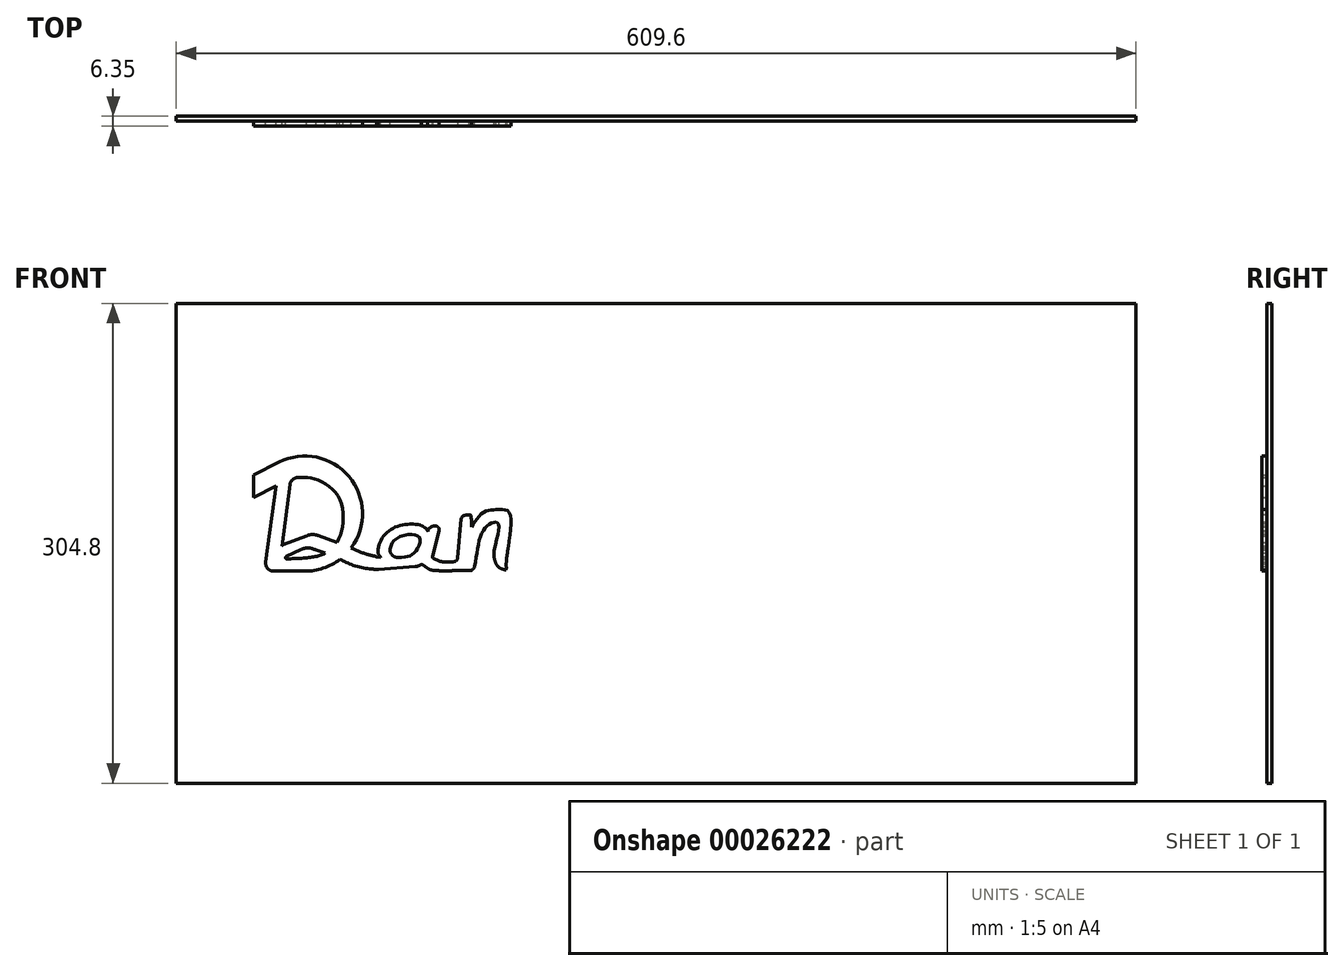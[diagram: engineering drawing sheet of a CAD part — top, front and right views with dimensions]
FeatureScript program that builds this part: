
annotation { "Feature Type Name" : "Feature", "Feature Type Description" : "" }
export const myFeature = defineFeature(function(context is Context, id is Id, definition is map)
    precondition{}
    {
        {
            var Q0;
            Q0=qCreatedBy(makeId("Front.planeOp"),FACE);
            var sketch = newSketch(context, id + "F0", { "sketchPlane" : qUnion([Q0])});
            skLineSegment(sketch, "E0.bottom", {"start": v(-304.36, 168.53) * mm, "end": v(305.24, 168.53) * mm});
            skLineSegment(sketch, "E0.top", {"start": v(-304.36, -136.27) * mm, "end": v(305.24, -136.27) * mm});
            skLineSegment(sketch, "E0.left", {"start": v(-304.36, 168.53) * mm, "end": v(-304.36, -136.27) * mm});
            skLineSegment(sketch, "E0.right", {"start": v(305.24, 168.53) * mm, "end": v(305.24, -136.27) * mm});
            skSolve(sketch);
        }
        {
            var Q0;
            Q0=makeQuery(id+"F0.imprint","IMPRINT",FACE,{"disambiguationData":[TD([[makeQuery(id+"F0.imprint","IMPRINT",EDGE,{"derivedFrom":sQuery(id+"F0.wireOp",EDGE,"E0.bottom")}),-1.0]])]});
            extrude(context, id + "F1", {"entities" : qUnion([Q0]), "depth" : 3.17 * mm});
        }
        {
            var Q0;
            Q0=makeQuery(id+"F1.opExtrude","CAP_FACE",FACE,{"disambiguationData":[OSD([sQuery(id+"F0.wireOp",EDGE,"E0.bottom"),sQuery(id+"F0.wireOp",EDGE,"E0.top"),sQuery(id+"F0.wireOp",EDGE,"E0.left"),sQuery(id+"F0.wireOp",EDGE,"E0.right")])],"isStart":false});
            var sketch = newSketch(context, id + "F2", { "sketchPlane" : qUnion([Q0])});
            skLineSegment(sketch, "E1", {"start": v(-258.66, -20.78) * mm, "end": v(-178.9, -20.78) * mm});
            skLineSegment(sketch, "E2", {"start": v(-178.9, -20.78) * mm, "end": v(-122.27, -20.78) * mm});
            skLineSegment(sketch, "E3", {"start": v(-122.27, -20.78) * mm, "end": v(-73.56, -20.78) * mm});
            skLineSegment(sketch, "E4", {"start": v(-73.56, -20.78) * mm, "end": v(-40.07, -20.78) * mm});
            skLineSegment(sketch, "E5", {"start": v(-40.07, -20.78) * mm, "end": v(1.94, -20.78) * mm});
            skLineSegment(sketch, "E6", {"start": v(1.94, -20.78) * mm, "end": v(38.48, -20.78) * mm});
            skLineSegment(sketch, "E7", {"start": v(104.84, -20.78) * mm, "end": v(209.57, -20.78) * mm});
            skLineSegment(sketch, "E8", {"start": v(-241.05, 52.49) * mm, "end": v(-247.54, 4.2) * mm});
            skLineSegment(sketch, "E9", {"start": v(-242.5, -1.56) * mm, "end": v(-222.66, -1.56) * mm});
            skArc(sketch, "E10", {"start": v(-222.66, -1.56) * mm, "mid": v(-210.96, 0.36) * mm, "end": v(-200.49, 5.93) * mm});
            skLineSegment(sketch, "E11", {"start": v(-239, 67.71) * mm, "end": v(-255.38, 59.52) * mm});
            skLineSegment(sketch, "E12", {"start": v(-258.22, 51) * mm, "end": v(-258.22, 51) * mm});
            skLineSegment(sketch, "E13", {"start": v(-249.7, 48.17) * mm, "end": v(-241.05, 52.49) * mm});
            skPoint(sketch, "E14.visualSharp", {"position": v(-261.06, 56.69) * mm});
            skLineSegment(sketch, "E14.filletArc", {"start": v(-255.38, 59.52) * mm, "end": v(-255.38, 59.52) * mm});
            skPoint(sketch, "E15.visualSharp", {"position": v(-255.38, 45.33) * mm});
            skLineSegment(sketch, "E16", {"start": v(-232.11, 53.5) * mm, "end": v(-237.18, 14.55) * mm});
            skFitSpline(sketch, "E17", {"points": [v(-231.6, 57.4) * mm, v(-217.7, 57.4) * mm, v(-201.48, 45.8) * mm, v(-199.6, 22.85) * mm, v(-210.9, 9.28) * mm, v(-238.3, 5.9) * mm], "startDerivative": vector(80.84, 11) * mm, "endDerivative": vector(-129.82, -10.44) * mm});
            skLineSegment(sketch, "E18", {"start": v(-214.13, 21.04) * mm, "end": v(-202.37, 16.67) * mm});
            skLineSegment(sketch, "E19", {"start": v(-234.45, 7.75) * mm, "end": v(-225.17, 12.17) * mm});
            skPoint(sketch, "E20.visualSharp", {"position": v(-219.31, 22.96) * mm});
            skArc(sketch, "E20.filletArc", {"start": v(-214.13, 21.04) * mm, "mid": v(-217.94, 21.67) * mm, "end": v(-221.7, 20.84) * mm});
            skPoint(sketch, "E21.visualSharp", {"position": v(-221.83, 13.76) * mm});
            skArc(sketch, "E21.filletArc", {"start": v(-215.7, 11.79) * mm, "mid": v(-220.38, 13.16) * mm, "end": v(-225.17, 12.17) * mm});
            skArc(sketch, "E22.filletArc", {"start": v(-234.45, 7.75) * mm, "mid": v(-234.9, 6.8) * mm, "end": v(-234.06, 6.19) * mm});
            skLineSegment(sketch, "E23", {"start": v(-236.14, 15.3) * mm, "end": v(-221.7, 20.84) * mm});
            skPoint(sketch, "E24.visualSharp", {"position": v(-238.12, 14.54) * mm});
            skArc(sketch, "E24.filletArc", {"start": v(-236.14, 15.3) * mm, "mid": v(-236.7, 15) * mm, "end": v(-237.18, 14.55) * mm});
            skPoint(sketch, "E25.visualSharp", {"position": v(-248.31, -1.56) * mm});
            skArc(sketch, "E25.filletArc", {"start": v(-247.54, 4.2) * mm, "mid": v(-246.33, 0.18) * mm, "end": v(-242.5, -1.56) * mm});
            skArc(sketch, "E26.filletArc", {"start": v(-227.57, 57.9) * mm, "mid": v(-230.61, 56.5) * mm, "end": v(-232.11, 53.5) * mm});
            skArc(sketch, "E27.trimOffspring", {"start": v(-193.22, 13.32) * mm, "mid": v(-194.68, 58.55) * mm, "end": v(-239, 67.71) * mm});
            skLineSegment(sketch, "E28", {"start": v(-248.31, -1.56) * mm, "end": v(-16.1, -1.56) * mm});
            skLineSegment(sketch, "E29", {"start": v(-174.55, 7.27) * mm, "end": v(-174.55, 7.27) * mm});
            skLineSegment(sketch, "E30", {"start": v(-144.66, 24.23) * mm, "end": v(-144.32, 23.55) * mm});
            skLineSegment(sketch, "E31", {"start": v(-144.66, 24.23) * mm, "end": v(-144.56, 24.4) * mm});
            skLineSegment(sketch, "E32", {"start": v(-140.06, 27.13) * mm, "end": v(-139.82, 27.13) * mm});
            skLineSegment(sketch, "E33", {"start": v(-137.36, 23.96) * mm, "end": v(-141.49, 7.85) * mm});
            skLineSegment(sketch, "E34", {"start": v(-175.71, -0.37) * mm, "end": v(-152.57, 1.35) * mm});
            skPoint(sketch, "E35.visualSharp", {"position": v(-171.6, 22.3) * mm});
            skPoint(sketch, "E36.visualSharp", {"position": v(-159.73, 28.33) * mm});
            skPoint(sketch, "E37.visualSharp", {"position": v(-146.1, 27.13) * mm});
            skArc(sketch, "E37.filletArc", {"start": v(-144.32, 23.55) * mm, "mid": v(-146, 25.78) * mm, "end": v(-148.38, 27.25) * mm});
            skFitSpline(sketch, "E38", {"points": [v(-177.38, 7.4) * mm, v(-174.92, 16.9) * mm, v(-168.37, 24.67) * mm, v(-158.5, 28.09) * mm, v(-148.48, 27.3) * mm, v(-145.04, 24.47) * mm], "startDerivative": vector(14.97, 44.13) * mm, "endDerivative": vector(24.1, -23.67) * mm});
            skPoint(sketch, "E36.filletArc.start.orphan", {"position": v(-158.5, 28.25) * mm});
            skArc(sketch, "E39.filletArc", {"start": v(-176.2, 12.3) * mm, "mid": v(-176.3, 11.09) * mm, "end": v(-176.1, 9.89) * mm});
            skFitSpline(sketch, "E40.trimOffspring", {"points": [v(-177.38, 7.4) * mm, v(-159.35, 7.4) * mm, v(-152.3, 11.02) * mm, v(-150.02, 20.15) * mm, v(-164, 19.4) * mm, v(-169.39, 7.4) * mm], "startDerivative": vector(65.48, -2.7) * mm, "endDerivative": vector(-5.68, -72.53) * mm});
            skArc(sketch, "E41.filletArc", {"start": v(-168.65, 12.49) * mm, "mid": v(-167.22, 8.64) * mm, "end": v(-163.42, 7.1) * mm});
            skPoint(sketch, "E42.visualSharp", {"position": v(-175.96, -0.4) * mm});
            skArc(sketch, "E42.filletArc", {"start": v(-175.88, -0.38) * mm, "mid": v(-175.8, -0.38) * mm, "end": v(-175.71, -0.37) * mm});
            skPoint(sketch, "E43.visualSharp", {"position": v(-151.52, 1.42) * mm});
            skArc(sketch, "E43.filletArc", {"start": v(-152.57, 1.35) * mm, "mid": v(-150.4, 1.83) * mm, "end": v(-148.46, 2.93) * mm});
            skLineSegment(sketch, "E44", {"start": v(-148.46, 2.93) * mm, "end": v(-143.95, -0.12) * mm});
            skLineSegment(sketch, "E45", {"start": v(-125.42, -1) * mm, "end": v(-118.5, -1) * mm});
            skPoint(sketch, "E46.visualSharp", {"position": v(-143.14, 27.13) * mm});
            skArc(sketch, "E46.filletArc", {"start": v(-140.06, 27.13) * mm, "mid": v(-142.7, 26.4) * mm, "end": v(-144.56, 24.4) * mm});
            skPoint(sketch, "E47.visualSharp", {"position": v(-136.55, 27.13) * mm});
            skArc(sketch, "E47.filletArc", {"start": v(-137.36, 23.96) * mm, "mid": v(-137.81, 26.15) * mm, "end": v(-139.82, 27.13) * mm});
            skLineSegment(sketch, "E48", {"start": v(-140.78, 6.37) * mm, "end": v(-137.44, 4.88) * mm});
            skLineSegment(sketch, "E49", {"start": v(-135.36, 4.44) * mm, "end": v(-128.15, 4.44) * mm});
            skPoint(sketch, "E50.visualSharp", {"position": v(-141.75, 6.8) * mm});
            skArc(sketch, "E50.filletArc", {"start": v(-141.49, 7.85) * mm, "mid": v(-141.4, 6.98) * mm, "end": v(-140.78, 6.37) * mm});
            skPoint(sketch, "E51.visualSharp", {"position": v(-136.45, 4.44) * mm});
            skArc(sketch, "E51.filletArc", {"start": v(-137.44, 4.88) * mm, "mid": v(-136.42, 4.55) * mm, "end": v(-135.36, 4.44) * mm});
            skPoint(sketch, "E52.visualSharp", {"position": v(-142.66, -1) * mm});
            skArc(sketch, "E52.filletArc", {"start": v(-143.95, -0.12) * mm, "mid": v(-142.6, -0.77) * mm, "end": v(-141.1, -1) * mm});
            skLineSegment(sketch, "E53", {"start": v(-125.62, 6.75) * mm, "end": v(-123.35, 31.61) * mm});
            skFitSpline(sketch, "E54", {"points": [v(-123.22, 33.06) * mm, v(-117.8, 34.24) * mm, v(-117.07, 33.06) * mm, v(-117.25, 0.6) * mm, v(-118.47, 0.65) * mm, v(-119.67, 0.72) * mm], "startDerivative": vector(22.26, 15.51) * mm, "endDerivative": vector(-0.04, -1.27) * mm});
            skArc(sketch, "E55.filletArc", {"start": v(-121.53, 33.82) * mm, "mid": v(-122.78, 33) * mm, "end": v(-123.35, 31.61) * mm});
            skFitSpline(sketch, "E56", {"points": [v(-116.66, 26.37) * mm, v(-109.03, 35.88) * mm, v(-100.72, 37.5) * mm, v(-92.58, 35.26) * mm, v(-94.73, 4.1) * mm, v(-95.63, -1.76) * mm, v(-102.81, -1.31) * mm, v(-103.75, 3.28) * mm], "startDerivative": vector(33.25, 69.65) * mm, "endDerivative": vector(14.9, 68.7) * mm});
            skFitSpline(sketch, "E57", {"points": [v(-118.5, -1) * mm, v(-116.53, -0.9) * mm, v(-114.8, 1.56) * mm], "startDerivative": vector(15.85, -0.5) * mm, "endDerivative": vector(2.08, 8.35) * mm});
            skFitSpline(sketch, "E58", {"points": [v(-114.8, 1.56) * mm, v(-110.55, 22.03) * mm, v(-104.07, 29) * mm, v(-99.86, 28.7) * mm, v(-103.75, 3.28) * mm], "startDerivative": vector(13.3, 66.56) * mm, "endDerivative": vector(-11.02, -98.62) * mm});
            skLineSegment(sketch, "E59", {"start": v(-215.7, 11.79) * mm, "end": v(-209.7, 9.85) * mm});
            skFitSpline(sketch, "E60", {"points": [v(-141.1, -1) * mm, v(-133.6, -1.4) * mm, v(-125.42, -1) * mm], "startDerivative": vector(15.17, -1.2) * mm, "endDerivative": vector(16.18, 1.19) * mm});
            skFitSpline(sketch, "E61", {"points": [v(-176.1, 9.89) * mm, v(-175.1, 8.08) * mm, v(-174.55, 7.27) * mm], "startDerivative": vector(0.37, -4.15) * mm, "endDerivative": vector(1.47, -2) * mm});
            skFitSpline(sketch, "E62", {"points": [v(-193.22, 13.32) * mm, v(-182.84, 9.1) * mm, v(-174.55, 7.27) * mm], "startDerivative": vector(18.02, -11.47) * mm, "endDerivative": vector(17.6, -2.48) * mm});
            skPoint(sketch, "E63.filletArc.start.orphan", {"position": v(-177.84, 7.6) * mm});
            skFitSpline(sketch, "E64", {"points": [v(-200.49, 5.93) * mm, v(-190.96, 1.92) * mm, v(-179.32, -0.32) * mm, v(-175.71, -0.37) * mm], "startDerivative": vector(23.23, -11.3) * mm, "endDerivative": vector(13.59, 0.56) * mm});
            skPoint(sketch, "E65.orphan", {"position": v(-177.2, -0.02) * mm});
            skLineSegment(sketch, "E66", {"start": v(-255.38, 59.52) * mm, "end": v(-255.38, 45.33) * mm});
            skLineSegment(sketch, "E67", {"start": v(-255.38, 45.33) * mm, "end": v(-249.7, 48.17) * mm});
            skLineSegment(sketch, "E68", {"start": v(-41.61, -1.56) * mm, "end": v(-22.9, -1.56) * mm});
            skLineSegment(sketch, "E69", {"start": v(26.94, -1.56) * mm, "end": v(3.48, -1.56) * mm});
            skPoint(sketch, "E70.visualSharp", {"position": v(-125.83, 4.44) * mm});
            skArc(sketch, "E70.filletArc", {"start": v(-128.15, 4.44) * mm, "mid": v(-126.44, 5.1) * mm, "end": v(-125.62, 6.75) * mm});
            skFitSpline(sketch, "E71", {"points": [v(-94.1, 9.75) * mm, v(-83.44, 6.64) * mm, v(-70.42, 10.65) * mm, v(-64.06, 33.22) * mm, v(-63.09, 35.02) * mm], "startDerivative": vector(36.38, -14.95) * mm, "endDerivative": vector(9.01, 9.22) * mm});
            skFitSpline(sketch, "E72", {"points": [v(-94.87, -0.81) * mm, v(-83.8, -1.04) * mm, v(-67.72, 0.93) * mm, v(-59.07, 25.1) * mm], "startDerivative": vector(38.4, -6.5) * mm, "endDerivative": vector(12.22, 74.4) * mm});
            skFitSpline(sketch, "E73", {"points": [v(-94.87, -0.81) * mm, v(-99.51, 0.94) * mm, v(-101.28, 3.28) * mm, v(-103.13, 7.6) * mm, v(-102.38, 11.5) * mm], "startDerivative": vector(-18.6, 2.38) * mm, "endDerivative": vector(1.13, 5.84) * mm});
            skLineSegment(sketch, "E74.trimOffspring", {"start": v(-94.87, -0.81) * mm, "end": v(-94.87, -0.81) * mm});
            skArc(sketch, "E75.filletArc", {"start": v(-93.46, 13.85) * mm, "mid": v(-92.8, 10.4) * mm, "end": v(-90.05, 8.23) * mm});
            skFitSpline(sketch, "E76", {"points": [v(-63.09, 35.02) * mm, v(-57.44, 36.05) * mm, v(-54.28, 35.02) * mm, v(-51.85, 11.25) * mm, v(-40.86, 6.71) * mm], "startDerivative": vector(31.2, 5.93) * mm, "endDerivative": vector(51.98, 11.21) * mm});
            skFitSpline(sketch, "E77", {"points": [v(-60.73, 15.8) * mm, v(-60.73, 5.25) * mm, v(-52.67, -0.47) * mm, v(-39.08, -0.61) * mm], "startDerivative": vector(-5.48, -36.42) * mm, "endDerivative": vector(39.62, 5.16) * mm});
            skLineSegment(sketch, "E78", {"start": v(-16.31, 5.69) * mm, "end": v(-15.07, 5.3) * mm});
            skFitSpline(sketch, "E79", {"points": [v(-39.08, -0.61) * mm, v(-20.1, 2.5) * mm, v(-0.98, 18.6) * mm, v(4.93, 31.72) * mm, v(0.26, 39.65) * mm, v(-18.15, 40.81) * mm, v(-33.46, 26.75) * mm, v(-36.41, 9.19) * mm], "startDerivative": vector(127, 3.04) * mm, "endDerivative": vector(-3.68, -124.36) * mm});
            skFitSpline(sketch, "E80", {"points": [v(-25.53, 9.5) * mm, v(-12.25, 19.21) * mm, v(-3.54, 28.85) * mm, v(-4.63, 33.2) * mm, v(-15.82, 31.95) * mm, v(-26, 22.48) * mm, v(-27.24, 10.98) * mm], "startDerivative": vector(66.91, 46.47) * mm, "endDerivative": vector(2.96, -70.75) * mm});
            skLineSegment(sketch, "E81", {"start": v(-40.86, 6.71) * mm, "end": v(-36.41, 8.24) * mm});
            skLineSegment(sketch, "E82", {"start": v(-25.56, 9.53) * mm, "end": v(-25.53, 9.5) * mm});
            skArc(sketch, "E83.filletArc", {"start": v(-27.32, 13.24) * mm, "mid": v(-27.07, 11.77) * mm, "end": v(-26.4, 10.44) * mm});
            skArc(sketch, "E84.filletArc", {"start": v(-26.4, 10.44) * mm, "mid": v(-25.57, 9.92) * mm, "end": v(-24.63, 10.13) * mm});
            skArc(sketch, "E85", {"start": v(-36.08, 15.9) * mm, "mid": v(-35.97, 12.14) * mm, "end": v(-34.46, 8.7) * mm});
            skLineSegment(sketch, "E86", {"start": v(-36.41, 8.24) * mm, "end": v(-34.46, 8.7) * mm});
            skFitSpline(sketch, "E87", {"points": [v(-102.38, 11.5) * mm, v(-102.38, 6.8) * mm, v(-101.28, 3.28) * mm], "startDerivative": vector(-0.62, -9.24) * mm, "endDerivative": vector(2.9, -7.16) * mm});
            skLineSegment(sketch, "E88.trimOffspring", {"start": v(-103.13, 7.6) * mm, "end": v(-103.13, 7.6) * mm});
            skLineSegment(sketch, "E89", {"start": v(22.18, -1.56) * mm, "end": v(3.48, -1.56) * mm});
            skLineSegment(sketch, "E90", {"start": v(-16.1, -1.56) * mm, "end": v(-22.72, 1.48) * mm});
            skFitSpline(sketch, "E91", {"points": [v(-13.76, 6.18) * mm, v(-0.92, 5.73) * mm, v(13.5, 11.45) * mm, v(30.63, 40.62) * mm, v(40.3, 65.41) * mm, v(47.88, 67.75) * mm, v(55.12, 60.88) * mm, v(49.49, 63.56) * mm], "startDerivative": vector(95.62, -9.36) * mm, "endDerivative": vector(-89.04, 54.07) * mm});
            skPoint(sketch, "E92.orphan", {"position": v(39.26, 69.05) * mm});
            skPoint(sketch, "E93.end.orphan", {"position": v(22.01, 12.18) * mm});
            skFitSpline(sketch, "E94", {"points": [v(47.88, 67.75) * mm, v(51.63, 63.85) * mm, v(42.08, 32.65) * mm, v(24.79, 2.29) * mm, v(-16.1, -1.56) * mm], "startDerivative": vector(43.08, -22.49) * mm, "endDerivative": vector(-149.36, 10.88) * mm});
            skFitSpline(sketch, "E95", {"points": [v(39.01, 24.47) * mm, v(42.4, 9.99) * mm, v(65.62, 8.76) * mm, v(69.83, 2.1) * mm, v(43.1, -1.56) * mm, v(32.43, 0.24) * mm, v(28.96, 5.78) * mm], "startDerivative": vector(-5.09, -108.3) * mm, "endDerivative": vector(-25.18, 56.89) * mm});
            skPoint(sketch, "E96.orphan", {"position": v(56.5, 66.44) * mm});
            skFitSpline(sketch, "E97.trimOffspring", {"points": [v(47.88, 67.75) * mm, v(51.63, 63.85) * mm, v(42.08, 32.65) * mm, v(24.79, 2.29) * mm, v(-16.1, -1.56) * mm], "startDerivative": vector(43.08, -22.49) * mm, "endDerivative": vector(-149.36, 10.88) * mm});
            skLineSegment(sketch, "E98.trimOffspring", {"start": v(14.2, -1.56) * mm, "end": v(202.51, -1.56) * mm});
            skSolve(sketch);
        }
        {
            var Q0;
            Q0=makeQuery(id+"F2.imprint","IMPRINT",FACE,{"disambiguationData":[TD([[makeQuery(id+"F2.imprint","IMPRINT",EDGE,{"derivedFrom":sQuery(id+"F2.wireOp",EDGE,"E8")}),1.0]])]});
            extrude(context, id + "F3", {"entities" : qUnion([Q0]), "operationType" : NewBodyOperationType.ADD, "depth" : 3.17 * mm});
        }
    });
